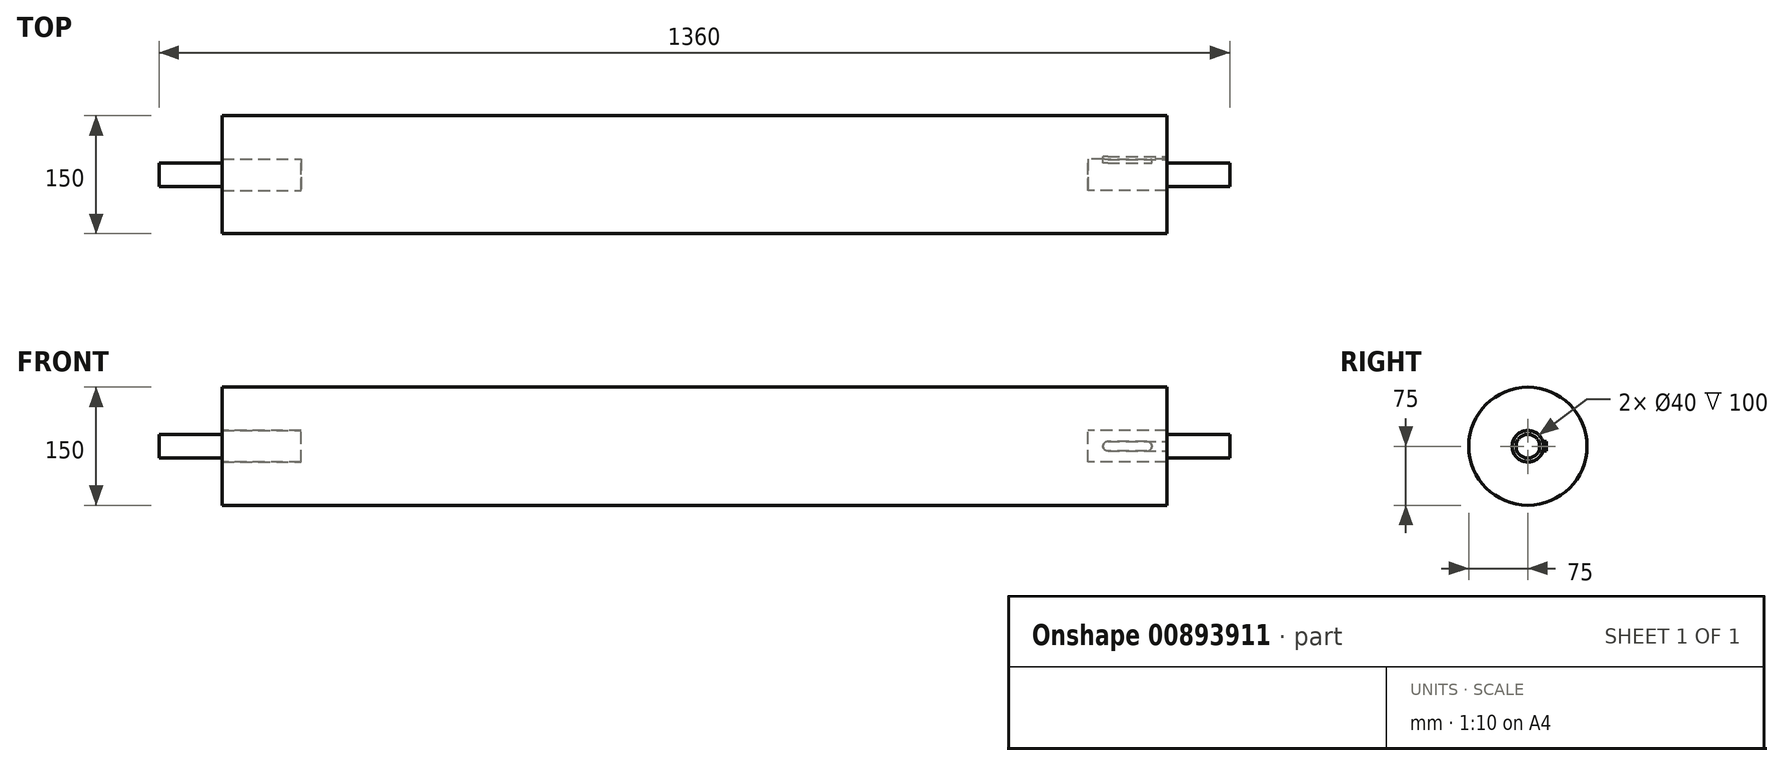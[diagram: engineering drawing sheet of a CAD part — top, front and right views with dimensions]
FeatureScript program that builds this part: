
annotation { "Feature Type Name" : "Feature", "Feature Type Description" : "" }
export const myFeature = defineFeature(function(context is Context, id is Id, definition is map)
    precondition{}
    {
        {
            var Q0;
            Q0=qCreatedBy(makeId("Right.planeOp"),FACE);
            var sketch = newSketch(context, id + "F0", { "sketchPlane" : qUnion([Q0])});
            skCircle(sketch, "E0", {"center": v(0, 0) * mm, "radius": 75 * mm});
            skSolve(sketch);
        }
        {
            var Q0;
            Q0=qSketchRegion(id+"F0",true);
            extrude(context, id + "F1", {"entities" : qUnion([Q0]), "endBound" : BoundingType.SYMMETRIC, "depth" : 1200 * mm, "offsetDistance" : 25 * mm});
        }
        {
            var Q0;
            Q0=makeQuery(id+"F1.opExtrude","CAP_FACE",FACE,{"disambiguationData":[OSD([sQuery(id+"F0.wireOp",EDGE,"E0")])],"isStart":false});
            var sketch = newSketch(context, id + "F2", { "sketchPlane" : qUnion([Q0])});
            skCircle(sketch, "E1", {"center": v(0, 0) * mm, "radius": 20 * mm});
            skSolve(sketch);
        }
        {
            var Q0;
            Q0=qSketchRegion(id+"F2",true);
            extrude(context, id + "F3", {"entities" : qUnion([Q0]), "operationType" : NewBodyOperationType.REMOVE, "oppositeDirection" : true, "depth" : 100 * mm, "offsetDistance" : 25 * mm});
        }
        {
            var Q0;
            Q0=makeQuery(id+"F1.opExtrude","CAP_FACE",FACE,{"disambiguationData":[OSD([sQuery(id+"F0.wireOp",EDGE,"E0")])],"isStart":true});
            var sketch = newSketch(context, id + "F4", { "sketchPlane" : qUnion([Q0])});
            skCircle(sketch, "E2", {"center": v(0, 0) * mm, "radius": 20 * mm});
            skSolve(sketch);
        }
        {
            var Q0;
            Q0=qSketchRegion(id+"F4",true);
            extrude(context, id + "F5", {"entities" : qUnion([Q0]), "operationType" : NewBodyOperationType.REMOVE, "oppositeDirection" : true, "depth" : 100 * mm, "offsetDistance" : 25 * mm});
        }
        {
            var Q0;
            Q0=makeQuery(id+"F1.opExtrude","CAP_FACE",FACE,{"disambiguationData":[OSD([sQuery(id+"F0.wireOp",EDGE,"E0")])],"isStart":false});
            var sketch = newSketch(context, id + "F6", { "sketchPlane" : qUnion([Q0])});
            skLineSegment(sketch, "E3.bottom", {"start": v(19.08, 6) * mm, "end": v(23.3, 6) * mm});
            skLineSegment(sketch, "E3.top", {"start": v(19.08, -6) * mm, "end": v(23.3, -6) * mm});
            skLineSegment(sketch, "E3.left", {"start": v(19.08, 6) * mm, "end": v(19.08, -6) * mm});
            skLineSegment(sketch, "E3.right", {"start": v(23.3, 6) * mm, "end": v(23.3, -6) * mm});
            skPoint(sketch, "E3.middle", {"position": v(21.19, 0) * mm});
            skSolve(sketch);
        }
        {
            var Q0;
            Q0=qSketchRegion(id+"F6",true);
            extrude(context, id + "F7", {"entities" : qUnion([Q0]), "operationType" : NewBodyOperationType.REMOVE, "oppositeDirection" : true, "depth" : 75 * mm, "offsetDistance" : 25 * mm});
        }
        {
            var Q0;
            Q0=makeQuery(id+"F3.boolean.opBoolean","COPY",FACE,{"derivedFrom":makeQuery(id+"F3.opExtrude","CAP_FACE",FACE,{"disambiguationData":[OSD([sQuery(id+"F2.wireOp",EDGE,"E1")])],"isStart":false})});
            var sketch = newSketch(context, id + "F8", { "sketchPlane" : qUnion([Q0])});
            skCircle(sketch, "E4", {"center": v(0, 0) * mm, "radius": 20 * mm});
            skSolve(sketch);
        }
        {
            var Q0;
            Q0=qSketchRegion(id+"F8",true);
            extrude(context, id + "F9", {"entities" : qUnion([Q0]), "depth" : 100 * mm, "offsetDistance" : 25 * mm});
        }
        {
            var Q0;
            Q0=makeQuery(id+"F9.opExtrude","CAP_FACE",FACE,{"disambiguationData":[OSD([sQuery(id+"F8.wireOp",EDGE,"E4")])],"isStart":false});
            var sketch = newSketch(context, id + "F10", { "sketchPlane" : qUnion([Q0])});
            skCircle(sketch, "E5", {"center": v(0, 0) * mm, "radius": 15 * mm});
            skSolve(sketch);
        }
        {
            var Q0;
            Q0=qSketchRegion(id+"F10",true);
            extrude(context, id + "F11", {"entities" : qUnion([Q0]), "operationType" : NewBodyOperationType.ADD, "depth" : 80 * mm, "offsetDistance" : 25 * mm});
        }
        {
            var Q0;
            Q0=makeQuery(id+"F9.opExtrude","SWEPT_BODY",BODY,{"disambiguationData":[OSD([sQuery(id+"F8.wireOp",EDGE,"E4")])]});
            var Q1;
            Q1=qCreatedBy(makeId("Right.planeOp"),FACE);
            mirror(context, id + "F12", {"entities" : qUnion([Q0]), "mirrorPlane" : qUnion([Q1])});
        }
        {
            var Q0;
            Q0=makeQuery(id+"F7.boolean.opBoolean","COPY",FACE,{"derivedFrom":makeQuery(id+"F7.opExtrude","SWEPT_FACE",FACE,{"disambiguationData":[OSD([sQuery(id+"F6.wireOp",EDGE,"E3.right")])]})});
            var sketch = newSketch(context, id + "F13", { "sketchPlane" : qUnion([Q0])});
            skLineSegment(sketch, "E6", {"start": v(525, 0) * mm, "end": v(575, 0) * mm});
            skArc(sketch, "E7.0.startCap", {"start": v(525, -6) * mm, "mid": v(519, 0) * mm, "end": v(525, 6) * mm});
            skArc(sketch, "E7.0.endCap", {"start": v(575, 6) * mm, "mid": v(581, 0) * mm, "end": v(575, -6) * mm});
            skLineSegment(sketch, "E7.0.left", {"start": v(525, 6) * mm, "end": v(575, 6) * mm});
            skLineSegment(sketch, "E7.0.right", {"start": v(525, -6) * mm, "end": v(575, -6) * mm});
            skSolve(sketch);
        }
        {
            var Q0;
            Q0=qSketchRegion(id+"F13",true);
            extrude(context, id + "F14", {"entities" : qUnion([Q0]), "operationType" : NewBodyOperationType.REMOVE, "depth" : 8.8 * mm, "offsetDistance" : 25 * mm});
        }
    });
